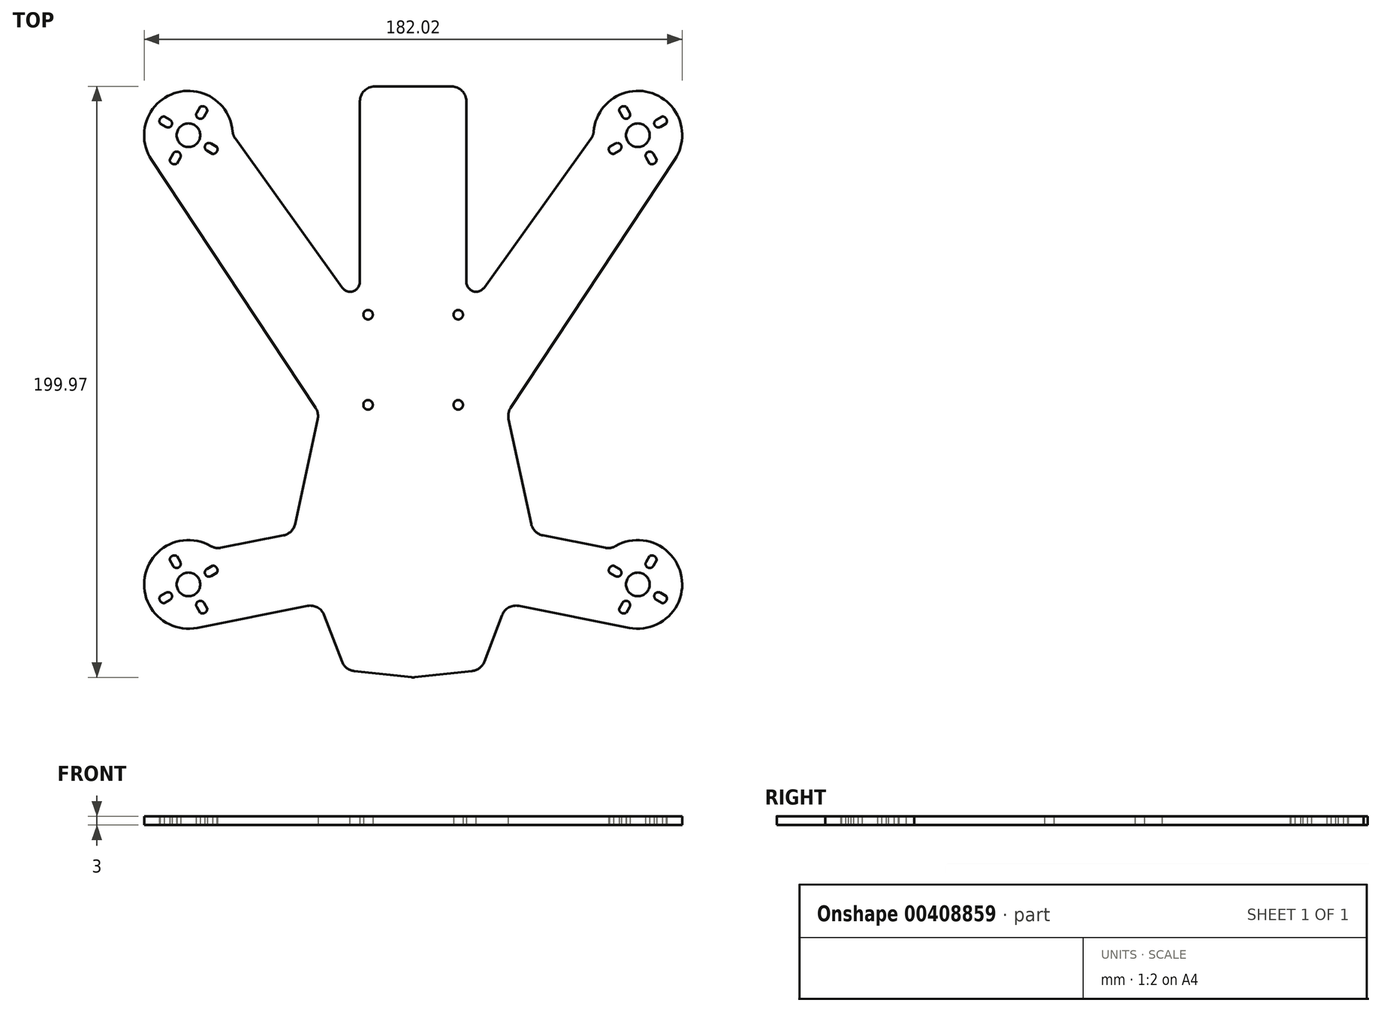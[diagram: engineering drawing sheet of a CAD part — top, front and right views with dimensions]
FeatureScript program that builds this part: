
annotation { "Feature Type Name" : "Feature", "Feature Type Description" : "" }
export const myFeature = defineFeature(function(context is Context, id is Id, definition is map)
    precondition{}
    {
        {
            var Q0;
            Q0=qCreatedBy(makeId("Top.planeOp"),FACE);
            var sketch = newSketch(context, id + "F0", { "sketchPlane" : qUnion([Q0])});
            skCircle(sketch, "E0", {"center": v(0, 0) * mm, "radius": 107.5 * mm, "construction": true});
            skLineSegment(sketch, "E1", {"start": v(0, -107.5) * mm, "end": v(0, 107.5) * mm, "construction": true});
            skLineSegment(sketch, "E2", {"start": v(-107.5, 0) * mm, "end": v(107.5, 0) * mm, "construction": true});
            skLineSegment(sketch, "E3", {"start": v(0, 0) * mm, "end": v(-76.01, 76.01) * mm, "construction": true});
            skCircle(sketch, "E4", {"center": v(-76.01, 76.01) * mm, "radius": 9.5 * mm, "construction": true});
            skCircle(sketch, "E5", {"center": v(-76.01, 76.01) * mm, "radius": 15 * mm});
            skLineSegment(sketch, "E6.bottom", {"start": v(18, 18) * mm, "end": v(-18, 18) * mm, "construction": true});
            skLineSegment(sketch, "E6.top", {"start": v(18, -18) * mm, "end": v(-18, -18) * mm, "construction": true});
            skLineSegment(sketch, "E6.left", {"start": v(18, 18) * mm, "end": v(18, -18) * mm, "construction": true});
            skLineSegment(sketch, "E6.right", {"start": v(-18, 18) * mm, "end": v(-18, -18) * mm});
            skCircle(sketch, "E7", {"center": v(-76.01, 76.01) * mm, "radius": 8 * mm, "construction": true});
            skLineSegment(sketch, "E8.bottom", {"start": v(15.25, 15.25) * mm, "end": v(-15.25, 15.25) * mm, "construction": true});
            skLineSegment(sketch, "E8.top", {"start": v(15.25, -15.25) * mm, "end": v(-15.25, -15.25) * mm, "construction": true});
            skLineSegment(sketch, "E8.left", {"start": v(15.25, 15.25) * mm, "end": v(15.25, -15.25) * mm, "construction": true});
            skLineSegment(sketch, "E8.right", {"start": v(-15.25, 15.25) * mm, "end": v(-15.25, -15.25) * mm, "construction": true});
            skCircle(sketch, "E9.MirrorC", {"center": v(76.01, 76.01) * mm, "radius": 15 * mm});
            skCircle(sketch, "E10.MirrorC", {"center": v(76.01, 76.01) * mm, "radius": 9.5 * mm, "construction": true});
            skCircle(sketch, "E11.MirrorC", {"center": v(76.01, 76.01) * mm, "radius": 8 * mm, "construction": true});
            skCircle(sketch, "E12.MirrorC", {"center": v(76.01, -76.01) * mm, "radius": 15 * mm});
            skCircle(sketch, "E13.MirrorC", {"center": v(76.01, -76.01) * mm, "radius": 9.5 * mm, "construction": true});
            skCircle(sketch, "E14.MirrorC", {"center": v(76.01, -76.01) * mm, "radius": 8 * mm, "construction": true});
            skCircle(sketch, "E15.MirrorC", {"center": v(-76.01, -76.01) * mm, "radius": 15 * mm});
            skCircle(sketch, "E16.MirrorC", {"center": v(-76.01, -76.01) * mm, "radius": 9.5 * mm, "construction": true});
            skCircle(sketch, "E17.MirrorC", {"center": v(-76.01, -76.01) * mm, "radius": 8 * mm, "construction": true});
            skLineSegment(sketch, "E18", {"start": v(-76.01, -91.01) * mm, "end": v(76.01, -91.01) * mm, "construction": true});
            skLineSegment(sketch, "E19", {"start": v(-23, 23) * mm, "end": v(-18, 23) * mm});
            skLineSegment(sketch, "E20", {"start": v(-23, 23) * mm, "end": v(-23, -105.01) * mm, "construction": true});
            skLineSegment(sketch, "E21", {"start": v(0, -107.5) * mm, "end": v(0, 92.5) * mm, "construction": true});
            skLineSegment(sketch, "E22", {"start": v(0, -107.5) * mm, "end": v(-23, -105.01) * mm});
            skLineSegment(sketch, "E23", {"start": v(-23, -105.01) * mm, "end": v(-90.03, 70.67) * mm, "construction": true});
            skLineSegment(sketch, "E24", {"start": v(76.01, -61.01) * mm, "end": v(-73.08, -90.72) * mm, "construction": true});
            skLineSegment(sketch, "E25", {"start": v(-23, -105.01) * mm, "end": v(-31.6, -82.46) * mm});
            skLineSegment(sketch, "E26", {"start": v(-31.6, -82.46) * mm, "end": v(-73.08, -90.72) * mm});
            skLineSegment(sketch, "E27", {"start": v(-61.01, 76.01) * mm, "end": v(-23, 23) * mm});
            skLineSegment(sketch, "E28", {"start": v(-40.64, -58.77) * mm, "end": v(-67, -64.02) * mm});
            skLineSegment(sketch, "E29", {"start": v(-18, 23) * mm, "end": v(-18, 92.5) * mm});
            skLineSegment(sketch, "E30", {"start": v(-18, 92.5) * mm, "end": v(0, 92.5) * mm});
            skLineSegment(sketch, "E31.MirrorCS", {"start": v(18, 92.5) * mm, "end": v(0, 92.5) * mm});
            skLineSegment(sketch, "E32.MirrorCS", {"start": v(18, 23) * mm, "end": v(18, 92.5) * mm});
            skLineSegment(sketch, "E33.MirrorCS", {"start": v(23, 23) * mm, "end": v(18, 23) * mm});
            skLineSegment(sketch, "E34.MirrorCS", {"start": v(61.01, 76.01) * mm, "end": v(23, 23) * mm});
            skLineSegment(sketch, "E35", {"start": v(-23, 23) * mm, "end": v(-40.64, -58.77) * mm, "construction": true});
            skLineSegment(sketch, "E36", {"start": v(-31.85, -18) * mm, "end": v(-40.64, -58.77) * mm});
            skLineSegment(sketch, "E37", {"start": v(-31.85, -18) * mm, "end": v(-88.53, 67.74) * mm});
            skLineSegment(sketch, "E38.MirrorCS", {"start": v(31.85, -18) * mm, "end": v(88.53, 67.74) * mm});
            skLineSegment(sketch, "E39.MirrorCS", {"start": v(23, 23) * mm, "end": v(40.64, -58.77) * mm, "construction": true});
            skLineSegment(sketch, "E40.MirrorCS", {"start": v(40.64, -58.77) * mm, "end": v(67, -64.02) * mm});
            skLineSegment(sketch, "E41.MirrorCS", {"start": v(-76.01, -61.01) * mm, "end": v(73.08, -90.72) * mm, "construction": true});
            skLineSegment(sketch, "E42.MirrorCS", {"start": v(23, -105.01) * mm, "end": v(90.03, 70.67) * mm, "construction": true});
            skLineSegment(sketch, "E43.MirrorCS", {"start": v(0, -107.5) * mm, "end": v(23, -105.01) * mm});
            skLineSegment(sketch, "E44", {"start": v(23, -105.01) * mm, "end": v(31.6, -82.46) * mm});
            skLineSegment(sketch, "E45", {"start": v(31.6, -82.46) * mm, "end": v(73.08, -90.72) * mm});
            skLineSegment(sketch, "E46", {"start": v(40.64, -58.77) * mm, "end": v(31.85, -18) * mm});
            skCircle(sketch, "E47", {"center": v(-15.25, 15.25) * mm, "radius": 1.6 * mm});
            skCircle(sketch, "E48.MirrorC", {"center": v(15.25, 15.25) * mm, "radius": 1.6 * mm});
            skCircle(sketch, "E49.MirrorC", {"center": v(15.25, -15.25) * mm, "radius": 1.6 * mm});
            skCircle(sketch, "E50.MirrorC", {"center": v(-15.25, -15.25) * mm, "radius": 1.6 * mm});
            skLineSegment(sketch, "E51", {"start": v(-61.01, 76.01) * mm, "end": v(-91.01, 76.01) * mm, "construction": true});
            skLineSegment(sketch, "E52", {"start": v(-76.01, 76.01) * mm, "end": v(-68.51, 89) * mm, "construction": true});
            skArc(sketch, "E53", {"start": v(-73.21, 83.64) * mm, "mid": v(-72.7, 81.74) * mm, "end": v(-70.81, 82.25) * mm});
            skLineSegment(sketch, "E54", {"start": v(-72.01, 82.94) * mm, "end": v(-69.23, 81.34) * mm, "construction": true});
            skLineSegment(sketch, "E55", {"start": v(-70.81, 82.25) * mm, "end": v(-69.66, 84.24) * mm});
            skLineSegment(sketch, "E56.MirrorCS", {"start": v(-73.21, 83.64) * mm, "end": v(-72.06, 85.63) * mm});
            skArc(sketch, "E57.trimOffspring", {"start": v(-69.66, 84.24) * mm, "mid": v(-70.46, 85.63) * mm, "end": v(-72.06, 85.63) * mm});
            skLineSegment(sketch, "E58.1.0", {"start": v(-83.64, 78.81) * mm, "end": v(-85.63, 79.96) * mm});
            skArc(sketch, "E58.1.1", {"start": v(-83.64, 78.81) * mm, "mid": v(-81.74, 79.32) * mm, "end": v(-82.25, 81.21) * mm});
            skArc(sketch, "E58.1.3", {"start": v(-84.24, 82.36) * mm, "mid": v(-85.63, 81.56) * mm, "end": v(-85.63, 79.96) * mm});
            skLineSegment(sketch, "E58.1.4", {"start": v(-82.25, 81.21) * mm, "end": v(-84.24, 82.36) * mm});
            skLineSegment(sketch, "E58.2.0", {"start": v(-78.81, 68.4) * mm, "end": v(-79.96, 66.4) * mm});
            skArc(sketch, "E58.2.1", {"start": v(-78.81, 68.4) * mm, "mid": v(-79.32, 70.29) * mm, "end": v(-81.21, 69.78) * mm});
            skArc(sketch, "E58.2.3", {"start": v(-82.36, 67.79) * mm, "mid": v(-81.56, 66.4) * mm, "end": v(-79.96, 66.4) * mm});
            skLineSegment(sketch, "E58.2.4", {"start": v(-81.21, 69.78) * mm, "end": v(-82.36, 67.79) * mm});
            skLineSegment(sketch, "E58.3.0", {"start": v(-68.4, 73.21) * mm, "end": v(-66.4, 72.06) * mm});
            skArc(sketch, "E58.3.1", {"start": v(-68.4, 73.21) * mm, "mid": v(-70.29, 72.7) * mm, "end": v(-69.78, 70.81) * mm});
            skArc(sketch, "E58.3.3", {"start": v(-67.79, 69.66) * mm, "mid": v(-66.4, 70.46) * mm, "end": v(-66.4, 72.06) * mm});
            skLineSegment(sketch, "E58.3.4", {"start": v(-69.78, 70.81) * mm, "end": v(-67.79, 69.66) * mm});
            skLineSegment(sketch, "E59.MirrorCS", {"start": v(70.81, 82.25) * mm, "end": v(69.66, 84.24) * mm});
            skArc(sketch, "E60.MirrorCS", {"start": v(69.66, 84.24) * mm, "mid": v(70.46, 85.63) * mm, "end": v(72.06, 85.63) * mm});
            skLineSegment(sketch, "E61.MirrorCS", {"start": v(73.21, 83.64) * mm, "end": v(72.06, 85.63) * mm});
            skArc(sketch, "E62.MirrorCS", {"start": v(73.21, 83.64) * mm, "mid": v(72.7, 81.74) * mm, "end": v(70.81, 82.25) * mm});
            skArc(sketch, "E63.MirrorCS", {"start": v(83.64, 78.81) * mm, "mid": v(81.74, 79.32) * mm, "end": v(82.25, 81.21) * mm});
            skLineSegment(sketch, "E64.MirrorCS", {"start": v(82.25, 81.21) * mm, "end": v(84.24, 82.36) * mm});
            skArc(sketch, "E65.MirrorCS", {"start": v(84.24, 82.36) * mm, "mid": v(85.63, 81.56) * mm, "end": v(85.63, 79.96) * mm});
            skLineSegment(sketch, "E66.MirrorCS", {"start": v(83.64, 78.81) * mm, "end": v(85.63, 79.96) * mm});
            skArc(sketch, "E67.MirrorCS", {"start": v(78.81, 68.4) * mm, "mid": v(79.32, 70.29) * mm, "end": v(81.21, 69.78) * mm});
            skLineSegment(sketch, "E68.MirrorCS", {"start": v(81.21, 69.78) * mm, "end": v(82.36, 67.79) * mm});
            skArc(sketch, "E69.MirrorCS", {"start": v(82.36, 67.79) * mm, "mid": v(81.56, 66.4) * mm, "end": v(79.96, 66.4) * mm});
            skLineSegment(sketch, "E70.MirrorCS", {"start": v(78.81, 68.4) * mm, "end": v(79.96, 66.4) * mm});
            skArc(sketch, "E71.MirrorCS", {"start": v(68.4, 73.21) * mm, "mid": v(70.29, 72.7) * mm, "end": v(69.78, 70.81) * mm});
            skLineSegment(sketch, "E72.MirrorCS", {"start": v(68.4, 73.21) * mm, "end": v(66.4, 72.06) * mm});
            skArc(sketch, "E73.MirrorCS", {"start": v(67.79, 69.66) * mm, "mid": v(66.4, 70.46) * mm, "end": v(66.4, 72.06) * mm});
            skLineSegment(sketch, "E74.MirrorCS", {"start": v(69.78, 70.81) * mm, "end": v(67.79, 69.66) * mm});
            skArc(sketch, "E75.MirrorCS", {"start": v(73.21, -83.64) * mm, "mid": v(72.7, -81.74) * mm, "end": v(70.81, -82.25) * mm});
            skArc(sketch, "E76.MirrorCS", {"start": v(83.64, -78.81) * mm, "mid": v(81.74, -79.32) * mm, "end": v(82.25, -81.21) * mm});
            skArc(sketch, "E77.MirrorCS", {"start": v(78.81, -68.4) * mm, "mid": v(79.32, -70.29) * mm, "end": v(81.21, -69.78) * mm});
            skArc(sketch, "E78.MirrorCS", {"start": v(68.4, -73.21) * mm, "mid": v(70.29, -72.7) * mm, "end": v(69.78, -70.81) * mm});
            skLineSegment(sketch, "E79.MirrorCS", {"start": v(70.81, -82.25) * mm, "end": v(69.66, -84.24) * mm});
            skLineSegment(sketch, "E80.MirrorCS", {"start": v(73.21, -83.64) * mm, "end": v(72.06, -85.63) * mm});
            skArc(sketch, "E81.MirrorCS", {"start": v(69.66, -84.24) * mm, "mid": v(70.46, -85.63) * mm, "end": v(72.06, -85.63) * mm});
            skLineSegment(sketch, "E82.MirrorCS", {"start": v(82.25, -81.21) * mm, "end": v(84.24, -82.36) * mm});
            skLineSegment(sketch, "E83.MirrorCS", {"start": v(83.64, -78.81) * mm, "end": v(85.63, -79.96) * mm});
            skArc(sketch, "E84.MirrorCS", {"start": v(84.24, -82.36) * mm, "mid": v(85.63, -81.56) * mm, "end": v(85.63, -79.96) * mm});
            skLineSegment(sketch, "E85.MirrorCS", {"start": v(81.21, -69.78) * mm, "end": v(82.36, -67.79) * mm});
            skLineSegment(sketch, "E86.MirrorCS", {"start": v(78.81, -68.4) * mm, "end": v(79.96, -66.4) * mm});
            skArc(sketch, "E87.MirrorCS", {"start": v(82.36, -67.79) * mm, "mid": v(81.56, -66.4) * mm, "end": v(79.96, -66.4) * mm});
            skLineSegment(sketch, "E88.MirrorCS", {"start": v(69.78, -70.81) * mm, "end": v(67.79, -69.66) * mm});
            skLineSegment(sketch, "E89.MirrorCS", {"start": v(68.4, -73.21) * mm, "end": v(66.4, -72.06) * mm});
            skArc(sketch, "E90.MirrorCS", {"start": v(67.79, -69.66) * mm, "mid": v(66.4, -70.46) * mm, "end": v(66.4, -72.06) * mm});
            skArc(sketch, "E91.MirrorCS", {"start": v(-69.66, -84.24) * mm, "mid": v(-70.46, -85.63) * mm, "end": v(-72.06, -85.63) * mm});
            skLineSegment(sketch, "E92.MirrorCS", {"start": v(-70.81, -82.25) * mm, "end": v(-69.66, -84.24) * mm});
            skArc(sketch, "E93.MirrorCS", {"start": v(-73.21, -83.64) * mm, "mid": v(-72.7, -81.74) * mm, "end": v(-70.81, -82.25) * mm});
            skLineSegment(sketch, "E94.MirrorCS", {"start": v(-73.21, -83.64) * mm, "end": v(-72.06, -85.63) * mm});
            skArc(sketch, "E95.MirrorCS", {"start": v(-83.64, -78.81) * mm, "mid": v(-81.74, -79.32) * mm, "end": v(-82.25, -81.21) * mm});
            skLineSegment(sketch, "E96.MirrorCS", {"start": v(-82.25, -81.21) * mm, "end": v(-84.24, -82.36) * mm});
            skLineSegment(sketch, "E97.MirrorCS", {"start": v(-83.64, -78.81) * mm, "end": v(-85.63, -79.96) * mm});
            skArc(sketch, "E98.MirrorCS", {"start": v(-84.24, -82.36) * mm, "mid": v(-85.63, -81.56) * mm, "end": v(-85.63, -79.96) * mm});
            skArc(sketch, "E99.MirrorCS", {"start": v(-68.4, -73.21) * mm, "mid": v(-70.29, -72.7) * mm, "end": v(-69.78, -70.81) * mm});
            skLineSegment(sketch, "E100.MirrorCS", {"start": v(-68.4, -73.21) * mm, "end": v(-66.4, -72.06) * mm});
            skLineSegment(sketch, "E101.MirrorCS", {"start": v(-69.78, -70.81) * mm, "end": v(-67.79, -69.66) * mm});
            skArc(sketch, "E102.MirrorCS", {"start": v(-67.79, -69.66) * mm, "mid": v(-66.4, -70.46) * mm, "end": v(-66.4, -72.06) * mm});
            skArc(sketch, "E103.MirrorCS", {"start": v(-78.81, -68.4) * mm, "mid": v(-79.32, -70.29) * mm, "end": v(-81.21, -69.78) * mm});
            skLineSegment(sketch, "E104.MirrorCS", {"start": v(-78.81, -68.4) * mm, "end": v(-79.96, -66.4) * mm});
            skLineSegment(sketch, "E105.MirrorCS", {"start": v(-81.21, -69.78) * mm, "end": v(-82.36, -67.79) * mm});
            skArc(sketch, "E106.MirrorCS", {"start": v(-82.36, -67.79) * mm, "mid": v(-81.56, -66.4) * mm, "end": v(-79.96, -66.4) * mm});
            skCircle(sketch, "E107", {"center": v(-76.01, 76.01) * mm, "radius": 4 * mm});
            skCircle(sketch, "E108.MirrorC", {"center": v(76.01, 76.01) * mm, "radius": 4 * mm});
            skCircle(sketch, "E109.MirrorC", {"center": v(76.01, -76.01) * mm, "radius": 4 * mm});
            skCircle(sketch, "E110.MirrorC", {"center": v(-76.01, -76.01) * mm, "radius": 4 * mm});
            skSolve(sketch);
        }
        {
            var Q0;
            Q0 = qSketchRegion(id + "F0", true);
            extrude(context, id + "F1", {"entities" : qUnion([Q0]), "depth" : 3 * mm});
        }
        {
            var Q0;
            Q0=makeQuery(id+"F1.opExtrude","SWEPT_EDGE",EDGE,{"disambiguationData":[OSD([sQuery(id+"F0.wireOp",EDGE,"E36"),sQuery(id+"F0.wireOp",EDGE,"E37")])]});
            var Q1;
            Q1=makeQuery(id+"F1.opExtrude","SWEPT_EDGE",EDGE,{"disambiguationData":[OSD([sQuery(id+"F0.wireOp",EDGE,"E38.MirrorCS"),sQuery(id+"F0.wireOp",EDGE,"E46")])]});
            var Q2;
            Q2=makeQuery(id+"F1.opExtrude","SWEPT_EDGE",EDGE,{"disambiguationData":[OSD([sQuery(id+"F0.wireOp",EDGE,"E40.MirrorCS"),sQuery(id+"F0.wireOp",EDGE,"E46")])]});
            var Q3;
            Q3=makeQuery(id+"F1.opExtrude","SWEPT_EDGE",EDGE,{"disambiguationData":[OSD([sQuery(id+"F0.wireOp",EDGE,"E28"),sQuery(id+"F0.wireOp",EDGE,"E36")])]});
            var Q4;
            Q4=makeQuery(id+"F1.opExtrude","SWEPT_EDGE",EDGE,{"disambiguationData":[OSD([sQuery(id+"F0.wireOp",EDGE,"E25"),sQuery(id+"F0.wireOp",EDGE,"E26")])]});
            var Q5;
            Q5=makeQuery(id+"F1.opExtrude","SWEPT_EDGE",EDGE,{"disambiguationData":[OSD([sQuery(id+"F0.wireOp",EDGE,"E44"),sQuery(id+"F0.wireOp",EDGE,"E45")])]});
            var Q6;
            Q6=makeQuery(id+"F1.opExtrude","SWEPT_EDGE",EDGE,{"disambiguationData":[OSD([sQuery(id+"F0.wireOp",EDGE,"E43.MirrorCS"),sQuery(id+"F0.wireOp",EDGE,"E44")])]});
            var Q7;
            Q7=makeQuery(id+"F1.opExtrude","SWEPT_EDGE",EDGE,{"disambiguationData":[OSD([sQuery(id+"F0.wireOp",EDGE,"E22"),sQuery(id+"F0.wireOp",EDGE,"E25")])]});
            var Q8;
            Q8=makeQuery(id+"F1.opExtrude","SWEPT_EDGE",EDGE,{"disambiguationData":[OSD([sQuery(id+"F0.wireOp",EDGE,"E22"),sQuery(id+"F0.wireOp",EDGE,"E43.MirrorCS")])]});
            var Q9;
            Q9=makeQuery(id+"F1.opExtrude","SWEPT_EDGE",EDGE,{"disambiguationData":[OSD([sQuery(id+"F0.wireOp",EDGE,"E12.MirrorC"),sQuery(id+"F0.wireOp",EDGE,"E40.MirrorCS")])]});
            var Q10;
            Q10=makeQuery(id+"F1.opExtrude","SWEPT_EDGE",EDGE,{"disambiguationData":[OSD([sQuery(id+"F0.wireOp",EDGE,"E15.MirrorC"),sQuery(id+"F0.wireOp",EDGE,"E28")])]});
            var Q11;
            Q11=makeQuery(id+"F1.opExtrude","SWEPT_EDGE",EDGE,{"disambiguationData":[OSD([sQuery(id+"F0.wireOp",EDGE,"E9.MirrorC"),sQuery(id+"F0.wireOp",EDGE,"E34.MirrorCS")])]});
            var Q12;
            Q12=makeQuery(id+"F1.opExtrude","SWEPT_EDGE",EDGE,{"disambiguationData":[OSD([sQuery(id+"F0.wireOp",EDGE,"E5"),sQuery(id+"F0.wireOp",EDGE,"E27")])]});
            var Q13;
            Q13=makeQuery(id+"F1.opExtrude","SWEPT_EDGE",EDGE,{"disambiguationData":[OSD([sQuery(id+"F0.wireOp",EDGE,"E31.MirrorCS"),sQuery(id+"F0.wireOp",EDGE,"E32.MirrorCS")])]});
            var Q14;
            Q14=makeQuery(id+"F1.opExtrude","SWEPT_EDGE",EDGE,{"disambiguationData":[OSD([sQuery(id+"F0.wireOp",EDGE,"E29"),sQuery(id+"F0.wireOp",EDGE,"E30")])]});
            fillet(context, id + "F2", {"entities" : qUnion([Q0, Q1, Q2, Q3, Q4, Q5, Q6, Q7, Q8, Q9, Q10, Q11, Q12, Q13, Q14]), "radius" : 5 * mm, "tangentPropagation" : true, "allowEdgeOverflow" : false});
        }
        {
            var Q0;
            Q0=makeQuery(id+"F1.opExtrude","SWEPT_EDGE",EDGE,{"disambiguationData":[OSD([sQuery(id+"F0.wireOp",EDGE,"E19"),sQuery(id+"F0.wireOp",EDGE,"E27")])]});
            var Q1;
            Q1=makeQuery(id+"F1.opExtrude","SWEPT_EDGE",EDGE,{"disambiguationData":[OSD([sQuery(id+"F0.wireOp",EDGE,"E19"),sQuery(id+"F0.wireOp",EDGE,"E29")])]});
            var Q2;
            Q2=makeQuery(id+"F1.opExtrude","SWEPT_EDGE",EDGE,{"disambiguationData":[OSD([sQuery(id+"F0.wireOp",EDGE,"E32.MirrorCS"),sQuery(id+"F0.wireOp",EDGE,"E33.MirrorCS")])]});
            var Q3;
            Q3=makeQuery(id+"F1.opExtrude","SWEPT_EDGE",EDGE,{"disambiguationData":[OSD([sQuery(id+"F0.wireOp",EDGE,"E33.MirrorCS"),sQuery(id+"F0.wireOp",EDGE,"E34.MirrorCS")])]});
            fillet(context, id + "F3", {"entities" : qUnion([Q0, Q1, Q2, Q3]), "radius" : 3.5 * mm, "tangentPropagation" : true, "allowEdgeOverflow" : false});
        }
    });
